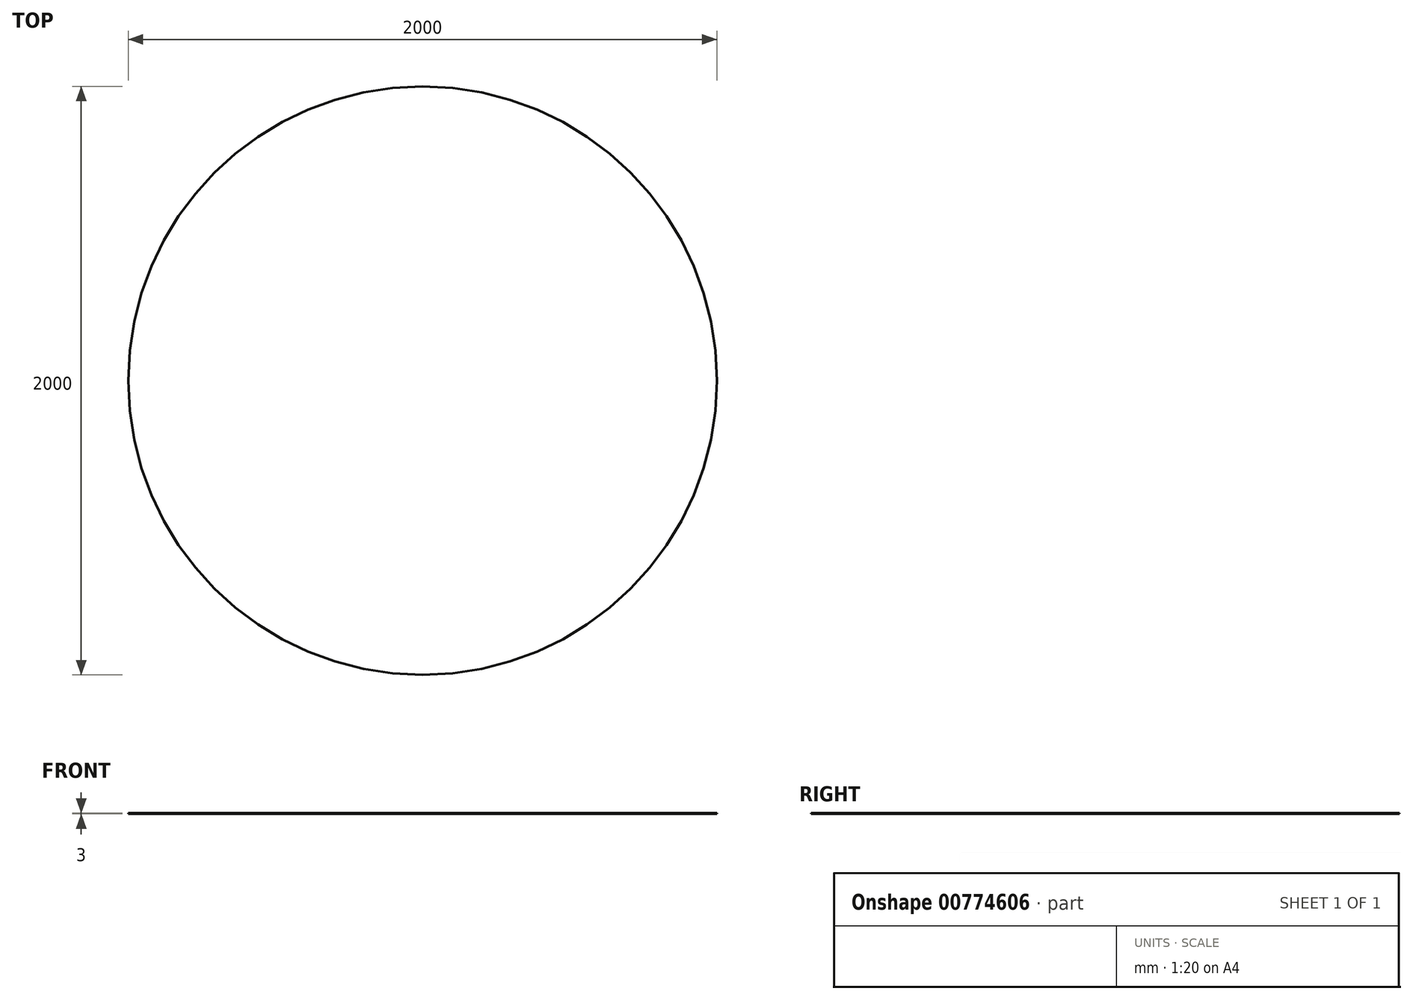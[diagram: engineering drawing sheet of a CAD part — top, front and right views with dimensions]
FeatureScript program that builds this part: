
annotation { "Feature Type Name" : "Feature", "Feature Type Description" : "" }
export const myFeature = defineFeature(function(context is Context, id is Id, definition is map)
    precondition{}
    {
        {
            var Q0;
            Q0=qCreatedBy(makeId("Top.planeOp"),FACE);
            var sketch = newSketch(context, id + "F0", { "sketchPlane" : qUnion([Q0])});
            skCircle(sketch, "E0", {"center": v(0, 0) * mm, "radius": 1000 * mm});
            skSolve(sketch);
        }
        {
            var Q0;
            Q0=makeQuery(id+"F0.imprint","IMPRINT",FACE,{"disambiguationData":[TD([[makeQuery(id+"F0.imprint","IMPRINT",EDGE,{"derivedFrom":sQuery(id+"F0.wireOp",EDGE,"E0")}),1.0]])]});
            extrude(context, id + "F1", {"entities" : qUnion([Q0]), "depth" : 3 * mm, "offsetDistance" : 25 * mm});
        }
    });
